# Revit family: Mixer-Sink-Dorf Villa
name_source: partatom
category: Plumbing Fixtures
revit_build: Autodesk Revit 2014 (Build: 20131024_2115(x64)
units: mm (PartAtom-declared; Revit-internal decimal feet)

## types (1)
- Standard
    Assembly Code = D2020300
    CW Connection = Yes
    CWFU = 1.98
    Connector Radius = 10 mm  [stored 0.0328084 ft]
    Cost = 0 $
    Default Elevation = 0 mm  [stored 0 ft]
    Description = Dorf Villa Sink Mixer
    HW Connection = Yes
    HWFU = 1.98
    Manufacturer = GWA Bathrooms & Kitchens
    Material_ANZRS = Metal-Chrome-Caroma
    Model = 6905.044A
    ModifiedIssue_ANZRS = 20140716 $
    Pressure Drop = 0.00 psi
    URL = http://www.dorf.com.au
    Vent Connection = No
    WELSRating_ANZRS = WELS 4 Star rated, 7.5L/min
    Waste Connection = No

note: [stored X ft] marks values corroborated as IEEE doubles in the binary element streams (Revit-internal decimal feet)

## geometry (parser evidence)
native form markers: Blend x8, Sweep x1
no freeform markers — native parametric forms only
